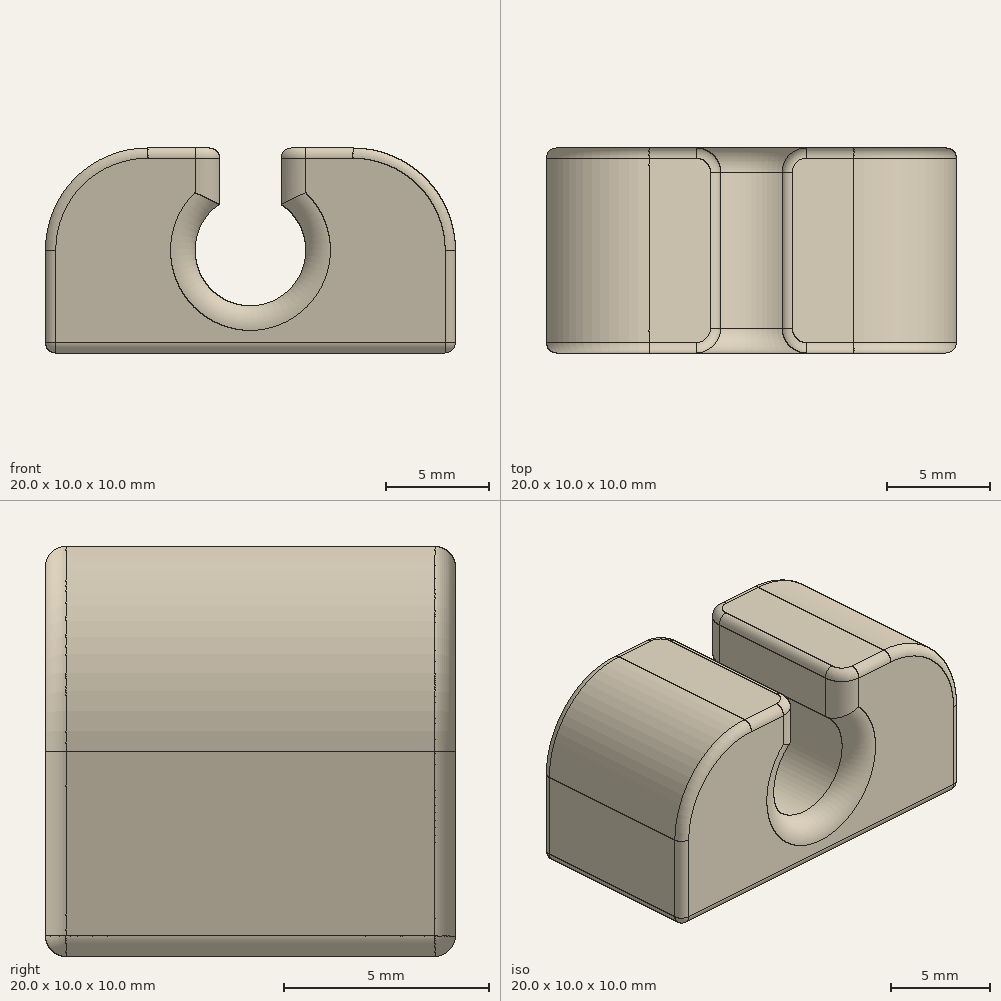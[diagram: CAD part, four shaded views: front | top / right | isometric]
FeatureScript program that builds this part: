
annotation { "Feature Type Name" : "Feature", "Feature Type Description" : "" }
export const myFeature = defineFeature(function(context is Context, id is Id, definition is map)
    precondition{}
    {
        {
            assignVariable(context, id + "F0", {"name" : "CableDiameter", "anyValue" : 3});
        }
        {
            var Q0;
            Q0=qCreatedBy(makeId("Front.planeOp"),FACE);
            var sketch = newSketch(context, id + "F1", { "sketchPlane" : qUnion([Q0])});
            skLineSegment(sketch, "E0.bottom", {"start": v(0, 20) * mm, "end": v(8.5, 20) * mm});
            skLineSegment(sketch, "E0.left", {"start": v(0, 20) * mm, "end": v(0, 10) * mm});
            skLineSegment(sketch, "E0.right", {"start": v(20, 20) * mm, "end": v(20, 10) * mm});
            skLineSegment(sketch, "E1", {"start": v(0, 10) * mm, "end": v(20, 10) * mm});
            skPoint(sketch, "E2", {"position": v(8.5, 20) * mm});
            skPoint(sketch, "E3", {"position": v(11.5, 20) * mm});
            skLineSegment(sketch, "E4.trimOffspring", {"start": v(11.5, 20) * mm, "end": v(20, 20) * mm});
            skArc(sketch, "E5", {"start": v(8.5, 17.24) * mm, "mid": v(10, 12.3) * mm, "end": v(11.5, 17.24) * mm});
            skLineSegment(sketch, "E6", {"start": v(10, 15) * mm, "end": v(10, 10) * mm, "construction": true});
            skLineSegment(sketch, "E7", {"start": v(10, 15) * mm, "end": v(10, 20) * mm, "construction": true});
            skLineSegment(sketch, "E8", {"start": v(8.5, 20) * mm, "end": v(8.5, 17.24) * mm});
            skLineSegment(sketch, "E9", {"start": v(11.5, 20) * mm, "end": v(11.5, 17.24) * mm});
            skSolve(sketch);
        }
        {
            var Q0;
            {var subQ0=sQuery(id+"F1.wireOp",EDGE,"E0.top");Q0=makeQuery(id+"F1.imprint","IMPRINT",FACE,{"disambiguationData":[TD([[makeQuery(id+"F1.imprint","IMPRINT",EDGE,{"derivedFrom":subQ0}),1.0]])]});}
            var Q1;
            Q1=makeQuery(id+"F1.imprint","IMPRINT",FACE,{"disambiguationData":[TD([[makeQuery(id+"F1.imprint","IMPRINT",EDGE,{"derivedFrom":sQuery(id+"F1.wireOp",EDGE,"E0.bottom")}),-1.0]])]});
            extrude(context, id + "F2", {"entities" : qUnion([Q0, Q1]), "depth" : 0.8 * mm, "offsetDistance" : 25 * mm});
        }
        {
            var Q0;
            {var subQ0=sQuery(id+"F1.wireOp",EDGE,"E1");Q0=makeQuery(id+"F1.imprint","IMPRINT",FACE,{"disambiguationData":[TD([[makeQuery(id+"F1.imprint","IMPRINT",EDGE,{"derivedFrom":subQ0}),1.0]])]});}
            extrude(context, id + "F3", {"entities" : qUnion([Q0]), "operationType" : NewBodyOperationType.ADD, "depth" : 10 * mm, "offsetDistance" : 25 * mm});
        }
        {
            var Q0;
            Q0=makeQuery(id+"F3.opExtrude","CAP_EDGE",EDGE,{"disambiguationData":[OSD([sQuery(id+"F1.wireOp",EDGE,"E5")])],"isStart":false});
            var Q1;
            Q1=makeQuery(id+"F3.opExtrude","CAP_EDGE",EDGE,{"disambiguationData":[OSD([sQuery(id+"F1.wireOp",EDGE,"E8")])],"isStart":false});
            var Q2;
            Q2=makeQuery(id+"F3.opExtrude","CAP_EDGE",EDGE,{"disambiguationData":[OSD([sQuery(id+"F1.wireOp",EDGE,"E9")])],"isStart":false});
            var Q3;
            Q3=makeQuery(id+"F3.opExtrude","CAP_EDGE",EDGE,{"disambiguationData":[OSD([sQuery(id+"F1.wireOp",EDGE,"E5")])],"isStart":true});
            var Q4;
            Q4=makeQuery(id+"F3.opExtrude","CAP_EDGE",EDGE,{"disambiguationData":[OSD([sQuery(id+"F1.wireOp",EDGE,"E8")])],"isStart":true});
            var Q5;
            Q5=makeQuery(id+"F3.opExtrude","CAP_EDGE",EDGE,{"disambiguationData":[OSD([sQuery(id+"F1.wireOp",EDGE,"E9")])],"isStart":true});
            var Q6;
            Q6=makeQuery(id+"F2.opExtrude","CAP_EDGE",EDGE,{"disambiguationData":[OSD([sQuery(id+"F1.wireOp",EDGE,"E9")])],"isStart":true});
            var Q7;
            Q7=makeQuery(id+"F2.opExtrude","CAP_EDGE",EDGE,{"disambiguationData":[OSD([sQuery(id+"F1.wireOp",EDGE,"E8")])],"isStart":true});
            var Q8;
            Q8=makeQuery(id+"F2.opExtrude","CAP_EDGE",EDGE,{"disambiguationData":[OSD([sQuery(id+"F1.wireOp",EDGE,"E5")])],"isStart":true});
            fillet(context, id + "F4", {"entities" : qUnion([Q0, Q1, Q2, Q3, Q4, Q5, Q6, Q7, Q8]), "radius" : 0.4 * (getVariable(context, 'CableDiameter')) * mm, "tangentPropagation" : true, "allowEdgeOverflow" : false});
        }
        {
            var Q0;
            {var subQ0=sQuery(id+"F1.wireOp",EDGE,"E4.trimOffspring");var subQ1=sQuery(id+"F1.wireOp",EDGE,"E0.right");Q0=makeQuery(id+"F3.boolean.opBoolean","MERGE",EDGE,{"derivedFrom":[makeQuery(id+"F2.opExtrude","SWEPT_EDGE",EDGE,{"disambiguationData":[OSD([subQ1,subQ0])]}),makeQuery(id+"F3.opExtrude","SWEPT_EDGE",EDGE,{"disambiguationData":[OSD([subQ1,subQ0])]})]});}
            var Q1;
            {var subQ0=sQuery(id+"F1.wireOp",EDGE,"E0.left");var subQ1=sQuery(id+"F1.wireOp",EDGE,"E0.bottom");Q1=makeQuery(id+"F3.boolean.opBoolean","MERGE",EDGE,{"derivedFrom":[makeQuery(id+"F2.opExtrude","SWEPT_EDGE",EDGE,{"disambiguationData":[OSD([subQ1,subQ0])]}),makeQuery(id+"F3.opExtrude","SWEPT_EDGE",EDGE,{"disambiguationData":[OSD([subQ1,subQ0])]})]});}
            fillet(context, id + "F5", {"entities" : qUnion([Q0, Q1]), "radius" : 5 * mm, "tangentPropagation" : true, "allowEdgeOverflow" : false});
        }
        {
            var Q0;
            {var subQ0=sQuery(id+"F1.wireOp",EDGE,"E0.left");var subQ1=sQuery(id+"F1.wireOp",EDGE,"E0.bottom");Q0=makeQuery(id+"F5.opFillet","BLEND_EDGE",EDGE,{"blendedFrom":[makeQuery(id+"F3.opExtrude","SWEPT_EDGE",EDGE,{"disambiguationData":[OSD([subQ1,subQ0])]}),makeQuery(id+"F3.opExtrude","CAP_FACE",FACE,{"disambiguationData":[OSD([subQ1,subQ0,sQuery(id+"F1.wireOp",EDGE,"E0.right"),sQuery(id+"F1.wireOp",EDGE,"E1"),sQuery(id+"F1.wireOp",EDGE,"E4.trimOffspring"),sQuery(id+"F1.wireOp",EDGE,"E5"),sQuery(id+"F1.wireOp",EDGE,"E8"),sQuery(id+"F1.wireOp",EDGE,"E9")])],"isStart":false})],"blendedInto":[makeQuery(id+"F3.opExtrude","CAP_FACE",FACE,{"disambiguationData":[OSD([subQ1,subQ0,sQuery(id+"F1.wireOp",EDGE,"E0.right"),sQuery(id+"F1.wireOp",EDGE,"E1"),sQuery(id+"F1.wireOp",EDGE,"E4.trimOffspring"),sQuery(id+"F1.wireOp",EDGE,"E5"),sQuery(id+"F1.wireOp",EDGE,"E8"),sQuery(id+"F1.wireOp",EDGE,"E9")])],"isStart":false})]});}
            var Q1;
            Q1=makeQuery(id+"F3.opExtrude","CAP_EDGE",EDGE,{"disambiguationData":[OSD([sQuery(id+"F1.wireOp",EDGE,"E0.left")])],"isStart":false});
            var Q2;
            Q2=makeQuery(id+"F3.opExtrude","CAP_EDGE",EDGE,{"disambiguationData":[OSD([sQuery(id+"F1.wireOp",EDGE,"E1")])],"isStart":false});
            var Q3;
            {var subQ0=sQuery(id+"F1.wireOp",EDGE,"E4.trimOffspring");var subQ1=sQuery(id+"F1.wireOp",EDGE,"E0.right");Q3=makeQuery(id+"F5.opFillet","BLEND_EDGE",EDGE,{"blendedFrom":[makeQuery(id+"F3.boolean.opBoolean","MERGE",EDGE,{"derivedFrom":[makeQuery(id+"F2.opExtrude","SWEPT_EDGE",EDGE,{"disambiguationData":[OSD([subQ1,subQ0])]}),makeQuery(id+"F3.opExtrude","SWEPT_EDGE",EDGE,{"disambiguationData":[OSD([subQ1,subQ0])]})]}),makeQuery(id+"F3.opExtrude","CAP_FACE",FACE,{"disambiguationData":[OSD([sQuery(id+"F1.wireOp",EDGE,"E0.bottom"),sQuery(id+"F1.wireOp",EDGE,"E0.left"),subQ1,sQuery(id+"F1.wireOp",EDGE,"E1"),subQ0,sQuery(id+"F1.wireOp",EDGE,"E5"),sQuery(id+"F1.wireOp",EDGE,"E8"),sQuery(id+"F1.wireOp",EDGE,"E9")])],"isStart":false})],"blendedInto":[makeQuery(id+"F3.opExtrude","CAP_FACE",FACE,{"disambiguationData":[OSD([sQuery(id+"F1.wireOp",EDGE,"E0.bottom"),sQuery(id+"F1.wireOp",EDGE,"E0.left"),subQ1,sQuery(id+"F1.wireOp",EDGE,"E1"),subQ0,sQuery(id+"F1.wireOp",EDGE,"E5"),sQuery(id+"F1.wireOp",EDGE,"E8"),sQuery(id+"F1.wireOp",EDGE,"E9")])],"isStart":false})]});}
            var Q4;
            {var subQ0=sQuery(id+"F1.wireOp",EDGE,"E4.trimOffspring");var subQ1=sQuery(id+"F1.wireOp",EDGE,"E0.right");Q4=makeQuery(id+"F5.opFillet","BLEND_EDGE",EDGE,{"blendedFrom":[makeQuery(id+"F3.boolean.opBoolean","MERGE",EDGE,{"derivedFrom":[makeQuery(id+"F2.opExtrude","SWEPT_EDGE",EDGE,{"disambiguationData":[OSD([subQ1,subQ0])]}),makeQuery(id+"F3.opExtrude","SWEPT_EDGE",EDGE,{"disambiguationData":[OSD([subQ1,subQ0])]})]}),makeQuery(id+"F2.opExtrude","CAP_FACE",FACE,{"disambiguationData":[OSD([sQuery(id+"F1.wireOp",EDGE,"E0.bottom"),sQuery(id+"F1.wireOp",EDGE,"E0.left"),subQ1,sQuery(id+"F1.wireOp",EDGE,"E1"),subQ0,sQuery(id+"F1.wireOp",EDGE,"E5"),sQuery(id+"F1.wireOp",EDGE,"E8"),sQuery(id+"F1.wireOp",EDGE,"E9")])],"isStart":true})],"blendedInto":[makeQuery(id+"F2.opExtrude","CAP_FACE",FACE,{"disambiguationData":[OSD([sQuery(id+"F1.wireOp",EDGE,"E0.bottom"),sQuery(id+"F1.wireOp",EDGE,"E0.left"),subQ1,sQuery(id+"F1.wireOp",EDGE,"E1"),subQ0,sQuery(id+"F1.wireOp",EDGE,"E5"),sQuery(id+"F1.wireOp",EDGE,"E8"),sQuery(id+"F1.wireOp",EDGE,"E9")])],"isStart":true})]});}
            var Q5;
            {var subQ0=sQuery(id+"F1.wireOp",EDGE,"E0.left");var subQ1=sQuery(id+"F1.wireOp",EDGE,"E0.bottom");Q5=makeQuery(id+"F5.opFillet","BLEND_EDGE",EDGE,{"blendedFrom":[makeQuery(id+"F3.boolean.opBoolean","MERGE",EDGE,{"derivedFrom":[makeQuery(id+"F2.opExtrude","SWEPT_EDGE",EDGE,{"disambiguationData":[OSD([subQ1,subQ0])]}),makeQuery(id+"F3.opExtrude","SWEPT_EDGE",EDGE,{"disambiguationData":[OSD([subQ1,subQ0])]})]}),makeQuery(id+"F2.opExtrude","CAP_FACE",FACE,{"disambiguationData":[OSD([subQ1,subQ0,sQuery(id+"F1.wireOp",EDGE,"E0.right"),sQuery(id+"F1.wireOp",EDGE,"E1"),sQuery(id+"F1.wireOp",EDGE,"E4.trimOffspring"),sQuery(id+"F1.wireOp",EDGE,"E5"),sQuery(id+"F1.wireOp",EDGE,"E8"),sQuery(id+"F1.wireOp",EDGE,"E9")])],"isStart":true})],"blendedInto":[makeQuery(id+"F2.opExtrude","CAP_FACE",FACE,{"disambiguationData":[OSD([subQ1,subQ0,sQuery(id+"F1.wireOp",EDGE,"E0.right"),sQuery(id+"F1.wireOp",EDGE,"E1"),sQuery(id+"F1.wireOp",EDGE,"E4.trimOffspring"),sQuery(id+"F1.wireOp",EDGE,"E5"),sQuery(id+"F1.wireOp",EDGE,"E8"),sQuery(id+"F1.wireOp",EDGE,"E9")])],"isStart":true})]});}
            var Q6;
            {var subQ0=sQuery(id+"F1.wireOp",EDGE,"E1");var subQ1=sQuery(id+"F1.wireOp",EDGE,"E0.right");Q6=makeQuery(id+"F3.boolean.opBoolean","MERGE",EDGE,{"derivedFrom":[makeQuery(id+"F2.opExtrude","SWEPT_EDGE",EDGE,{"disambiguationData":[OSD([subQ1,subQ0])]}),makeQuery(id+"F3.opExtrude","SWEPT_EDGE",EDGE,{"disambiguationData":[OSD([subQ1,subQ0])]})]});}
            var Q7;
            {var subQ0=sQuery(id+"F1.wireOp",EDGE,"E1");var subQ1=sQuery(id+"F1.wireOp",EDGE,"E0.left");Q7=makeQuery(id+"F3.boolean.opBoolean","MERGE",EDGE,{"derivedFrom":[makeQuery(id+"F2.opExtrude","SWEPT_EDGE",EDGE,{"disambiguationData":[OSD([subQ1,subQ0])]}),makeQuery(id+"F3.opExtrude","SWEPT_EDGE",EDGE,{"disambiguationData":[OSD([subQ1,subQ0])]})]});}
            var Q8;
            Q8=makeQuery(id+"F2.opExtrude","CAP_EDGE",EDGE,{"disambiguationData":[OSD([sQuery(id+"F1.wireOp",EDGE,"E1")])],"isStart":true});
            fillet(context, id + "F6", {"entities" : qUnion([Q0, Q1, Q2, Q3, Q4, Q5, Q6, Q7, Q8]), "radius" : 0.5 * mm, "tangentPropagation" : true, "allowEdgeOverflow" : false});
        }
    });
